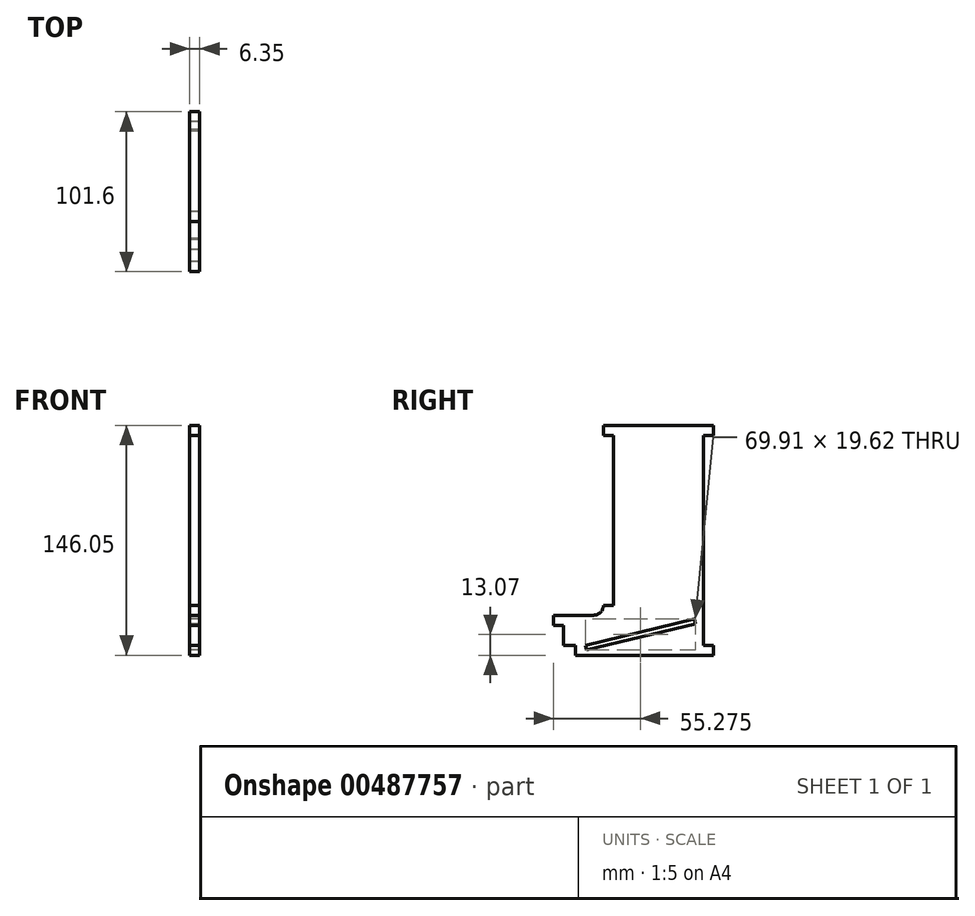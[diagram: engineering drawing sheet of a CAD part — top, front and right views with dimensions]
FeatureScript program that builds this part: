
annotation { "Feature Type Name" : "Feature", "Feature Type Description" : "" }
export const myFeature = defineFeature(function(context is Context, id is Id, definition is map)
    precondition{}
    {
        {
            var Q0;
            Q0=qCreatedBy(makeId("Right.planeOp"),FACE);
            var sketch = newSketch(context, id + "F0", { "sketchPlane" : qUnion([Q0])});
            skLineSegment(sketch, "E0.bottom", {"start": v(0, 0) * mm, "end": v(-69.85, 0) * mm});
            skLineSegment(sketch, "E0.top", {"start": v(0, 146.05) * mm, "end": v(-69.85, 146.05) * mm});
            skLineSegment(sketch, "E0.left", {"start": v(0, 0) * mm, "end": v(0, 146.05) * mm});
            skLineSegment(sketch, "E0.right", {"start": v(-69.85, 0) * mm, "end": v(-69.85, 146.05) * mm});
            skLineSegment(sketch, "E1.bottom", {"start": v(-69.85, 0) * mm, "end": v(-101.6, 0) * mm});
            skLineSegment(sketch, "E1.top", {"start": v(-69.85, 25.4) * mm, "end": v(-101.6, 25.4) * mm});
            skLineSegment(sketch, "E1.left", {"start": v(-69.85, 0) * mm, "end": v(-69.85, 25.4) * mm});
            skLineSegment(sketch, "E1.right", {"start": v(-101.6, 0) * mm, "end": v(-101.6, 25.4) * mm});
            skSolve(sketch);
        }
        {
            var Q0;
            Q0 = qSketchRegion(id + "F0", true);
            extrude(context, id + "F1", {"entities" : qUnion([Q0]), "depth" : 6.35 * mm});
        }
        {
            var Q0;
            Q0=qCreatedBy(makeId("Right.planeOp"),FACE);
            var sketch = newSketch(context, id + "F2", { "sketchPlane" : qUnion([Q0])});
            skLineSegment(sketch, "E2.bottom", {"start": v(0, 6.35) * mm, "end": v(-6.35, 6.35) * mm});
            skLineSegment(sketch, "E2.top", {"start": v(0, 139.7) * mm, "end": v(-6.35, 139.7) * mm});
            skLineSegment(sketch, "E2.left", {"start": v(0, 6.35) * mm, "end": v(0, 139.7) * mm});
            skLineSegment(sketch, "E2.right", {"start": v(-6.35, 6.35) * mm, "end": v(-6.35, 139.7) * mm});
            skSolve(sketch);
        }
        {
            var Q0;
            Q0 = qSketchRegion(id + "F2", true);
            extrude(context, id + "F3", {"entities" : qUnion([Q0]), "operationType" : NewBodyOperationType.REMOVE, "depth" : 12.45 * mm});
        }
        {
            var Q0;
            Q0=qCreatedBy(makeId("Right.planeOp"),FACE);
            var sketch = newSketch(context, id + "F4", { "sketchPlane" : qUnion([Q0])});
            skLineSegment(sketch, "E3.bottom", {"start": v(-63.5, 139.7) * mm, "end": v(-69.85, 139.7) * mm});
            skLineSegment(sketch, "E3.top", {"start": v(-63.5, 31.75) * mm, "end": v(-69.85, 31.75) * mm});
            skLineSegment(sketch, "E3.left", {"start": v(-63.5, 139.7) * mm, "end": v(-63.5, 31.75) * mm});
            skLineSegment(sketch, "E3.right", {"start": v(-69.85, 139.7) * mm, "end": v(-69.85, 31.75) * mm});
            skPoint(sketch, "E3.middle", {"position": v(-66.68, 85.73) * mm});
            skSolve(sketch);
        }
        {
            var Q0;
            Q0 = qSketchRegion(id + "F4", true);
            extrude(context, id + "F5", {"entities" : qUnion([Q0]), "operationType" : NewBodyOperationType.REMOVE, "depth" : 9.9 * mm});
        }
        {
            var Q0;
            Q0=qCreatedBy(makeId("Right.planeOp"),FACE);
            var sketch = newSketch(context, id + "F6", { "sketchPlane" : qUnion([Q0])});
            skLineSegment(sketch, "E4.bottom", {"start": v(-101.6, 19.05) * mm, "end": v(-95.25, 19.05) * mm});
            skLineSegment(sketch, "E4.top", {"start": v(-101.6, 0) * mm, "end": v(-95.25, 0) * mm});
            skLineSegment(sketch, "E4.left", {"start": v(-101.6, 19.05) * mm, "end": v(-101.6, 0) * mm});
            skLineSegment(sketch, "E4.right", {"start": v(-95.25, 19.05) * mm, "end": v(-95.25, 0) * mm});
            skLineSegment(sketch, "E5.bottom", {"start": v(-87.63, 6.35) * mm, "end": v(-95.25, 6.35) * mm});
            skLineSegment(sketch, "E5.top", {"start": v(-87.63, 0) * mm, "end": v(-95.25, 0) * mm});
            skLineSegment(sketch, "E5.left", {"start": v(-87.63, 6.35) * mm, "end": v(-87.63, 0) * mm});
            skLineSegment(sketch, "E5.right", {"start": v(-95.25, 6.35) * mm, "end": v(-95.25, 0) * mm});
            skPoint(sketch, "E5.middle", {"position": v(-91.44, 3.18) * mm});
            skSolve(sketch);
        }
        {
            var Q0;
            Q0 = qSketchRegion(id + "F6", true);
            extrude(context, id + "F7", {"entities" : qUnion([Q0]), "operationType" : NewBodyOperationType.REMOVE, "depth" : 10.67 * mm});
        }
        {
            var Q0;
            Q0=qCreatedBy(makeId("Right.planeOp"),FACE);
            var sketch = newSketch(context, id + "F8", { "sketchPlane" : qUnion([Q0])});
            skLineSegment(sketch, "E6.bottom", {"start": v(-69.85, 25.4) * mm, "end": v(-76.2, 25.4) * mm});
            skLineSegment(sketch, "E6.top", {"start": v(-69.85, 31.75) * mm, "end": v(-76.2, 31.75) * mm});
            skLineSegment(sketch, "E6.left", {"start": v(-69.85, 25.4) * mm, "end": v(-69.85, 31.75) * mm});
            skLineSegment(sketch, "E6.right", {"start": v(-76.2, 25.4) * mm, "end": v(-76.2, 31.75) * mm});
            skSolve(sketch);
        }
        {
            var Q0;
            Q0 = qSketchRegion(id + "F8", true);
            extrude(context, id + "F9", {"entities" : qUnion([Q0]), "operationType" : NewBodyOperationType.ADD, "depth" : 6.35 * mm});
        }
        {
            var Q0;
            Q0=qCreatedBy(makeId("Right.planeOp"),FACE);
            var sketch = newSketch(context, id + "F10", { "sketchPlane" : qUnion([Q0])});
            skCircle(sketch, "E7", {"center": v(-76.2, 31.75) * mm, "radius": 6.35 * mm});
            skSolve(sketch);
        }
        {
            var Q0;
            Q0 = qSketchRegion(id + "F10", true);
            extrude(context, id + "F11", {"entities" : qUnion([Q0]), "operationType" : NewBodyOperationType.REMOVE, "depth" : 8.94 * mm});
        }
        {
            var Q0;
            Q0=makeQuery(id+"F9.boolean.opBoolean","MERGE",FACE,{"derivedFrom":[makeQuery(id+"F1.opExtrude","CAP_FACE",FACE,{"disambiguationData":[OSD([sQuery(id+"F0.wireOp",EDGE,"E0.bottom"),sQuery(id+"F0.wireOp",EDGE,"E0.top"),sQuery(id+"F0.wireOp",EDGE,"E0.left"),sQuery(id+"F0.wireOp",EDGE,"E0.right"),sQuery(id+"F0.wireOp",EDGE,"E1.bottom"),sQuery(id+"F0.wireOp",EDGE,"E1.top"),sQuery(id+"F0.wireOp",EDGE,"E1.right")])],"isStart":true}),makeQuery(id+"F9.opExtrude","CAP_FACE",FACE,{"disambiguationData":[OSD([sQuery(id+"F8.wireOp",EDGE,"E6.bottom"),sQuery(id+"F8.wireOp",EDGE,"E6.top"),sQuery(id+"F8.wireOp",EDGE,"E6.left"),sQuery(id+"F8.wireOp",EDGE,"E6.right")])],"isStart":true})]});
            var sketch = newSketch(context, id + "F12", { "sketchPlane" : qUnion([Q0])});
            skLineSegment(sketch, "E8", {"start": v(81.28, 6.35) * mm, "end": v(12.1, 22.88) * mm});
            skLineSegment(sketch, "E9", {"start": v(12.1, 22.88) * mm, "end": v(11.37, 19.8) * mm});
            skLineSegment(sketch, "E10", {"start": v(11.37, 19.8) * mm, "end": v(80.54, 3.26) * mm});
            skLineSegment(sketch, "E11", {"start": v(80.54, 3.26) * mm, "end": v(81.28, 6.35) * mm});
            skSolve(sketch);
        }
        {
            var Q0;
            Q0 = qSketchRegion(id + "F12", true);
            extrude(context, id + "F13", {"entities" : qUnion([Q0]), "operationType" : NewBodyOperationType.REMOVE, "endBound" : BoundingType.THROUGH_ALL, "oppositeDirection" : true, "depth" : 25.4 * mm});
        }
    });
